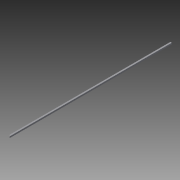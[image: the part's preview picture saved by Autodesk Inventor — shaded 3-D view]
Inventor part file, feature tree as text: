
AUTODESK INVENTOR PART (.ipt)
format: ipt  version: 2015 SP1 (Build 190203100, 203)  size: 77,312 bytes
history: native  units: mm
features: other x3, sketch x2
ambient origin geometry x8: Origin, YZ Plane, XZ Plane, XY Plane, X Axis, Y Axis, Z Axis, Center Point
bodies: Solid1 (feature_tree)
feature tree (5):
  other  "Pied.ipt"
  other  "Solid1::Pied.ipt"
  other  "TaggingFeature1"
  sketch  "Sketch1"  dims[d0=10.0mm]
  sketch  "Sketch2"
